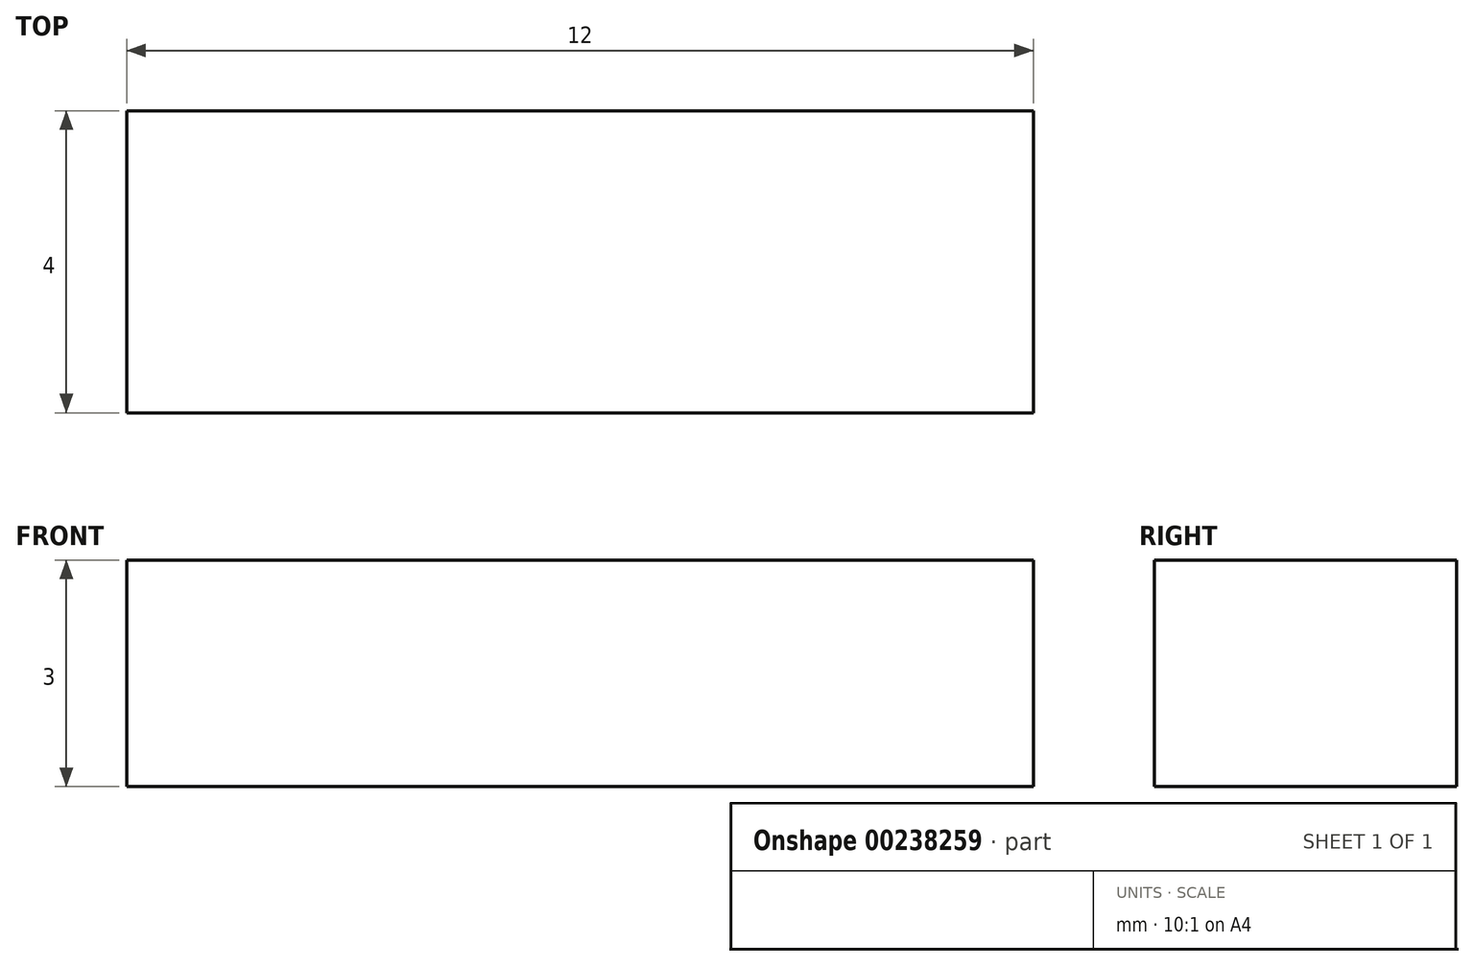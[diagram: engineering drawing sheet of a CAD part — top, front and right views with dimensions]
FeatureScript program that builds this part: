
annotation { "Feature Type Name" : "Feature", "Feature Type Description" : "" }
export const myFeature = defineFeature(function(context is Context, id is Id, definition is map)
    precondition{}
    {
        {
            var Q0;
            Q0=qCreatedBy(makeId("Top.planeOp"),FACE);
            var sketch = newSketch(context, id + "F0", { "sketchPlane" : qUnion([Q0])});
            skLineSegment(sketch, "E0.bottom", {"start": v(6, -2) * mm, "end": v(-6, -2) * mm});
            skLineSegment(sketch, "E0.top", {"start": v(6, 2) * mm, "end": v(-6, 2) * mm});
            skLineSegment(sketch, "E0.left", {"start": v(6, -2) * mm, "end": v(6, 2) * mm});
            skLineSegment(sketch, "E0.right", {"start": v(-6, -2) * mm, "end": v(-6, 2) * mm});
            skPoint(sketch, "E0.middle", {"position": v(0, 0) * mm});
            skSolve(sketch);
        }
        {
            var Q0;
            Q0=makeQuery(id+"F0.imprint","IMPRINT",FACE,{"disambiguationData":[TD([[makeQuery(id+"F0.imprint","IMPRINT",EDGE,{"derivedFrom":sQuery(id+"F0.wireOp",EDGE,"E0.bottom")}),-1.0]])]});
            extrude(context, id + "F1", {"entities" : qUnion([Q0]), "depth" : 3 * mm});
        }
    });
